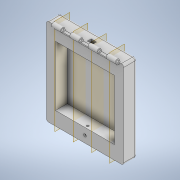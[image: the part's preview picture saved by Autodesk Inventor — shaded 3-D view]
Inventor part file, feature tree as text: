
AUTODESK INVENTOR PART (.ipt)
format: ipt  version: 2022 (Build 260153000, 153)  size: 294,912 bytes
history: native  units: in
note: dims shown in document units (in); Inventor stores cm internally (conversion verified against a paired STEP export)
features: extrude x13, sketch x13, plane x4, fillet x3, projected_geometry x3
ambient origin geometry x8: Origin, YZ Plane, XZ Plane, XY Plane, X Axis, Y Axis, Z Axis, Center Point
bodies: Solid1 (feature_tree)
feature tree (36):
  extrude  "Extrusion1"  Depth=6.6in
  extrude  "Extrusion3"  Depth=1.5in
  fillet  "Fillet1"  Radius=1.0in
  plane  "Work Plane1"
  extrude  "Extrusion4"  Depth=1.48in TaperAngle=0.0deg
  plane  "Work Plane2"
  extrude  "Extrusion5"  Depth=0.25in
  plane  "Work Plane3"
  extrude  "Extrusion6"  Depth=0.45in
  plane  "Work Plane4"
  extrude  "Extrusion7"  Depth=0.26in
  extrude  "Extrusion8"  Depth=2.01in
  extrude  "Extrusion9"  Depth=0.45in
  fillet  "Fillet2"  Radius=0.26in
  fillet  "Fillet3"  Radius=1.0in
  extrude  "Extrusion10"  Depth=0.45in
  extrude  "Extrusion11"  Depth=0.26in
  extrude  "Extrusion12"  Depth=2.01in
  extrude  "Extrusion14"  Depth=0.45in
  extrude  "Extrusion15"  Depth=0.6in TaperAngle=0.0deg
  sketch  "Sketch1"  dims[d0=6.506in d1=6.6in]
  sketch  "Sketch3"  dims[d2=1.5in d3=1.5in d4=1.0in]
  sketch  "Sketch4"  dims[d5=1.0in d6=1.48in d7=0.0in]
  sketch  "Sketch5"  dims[d10=0.185in d11=0.0in d12=0.25in]
  sketch  "Sketch6"  dims[d13=0.01in d14=0.45in]
  sketch  "Sketch7"  dims[d15=0.45in d16=0.26in]
  sketch  "Sketch9"  dims[d17=1.0in d18=0.0in d19=2.01in]
  sketch  "Sketch10"  dims[d20=0.45in d21=0.45in d22=0.26in d23=1.0in d24=0.0in]
  projected_geometry  "Projected Loop1"
  sketch  "Sketch11"  dims[d25=2.01in d26=0.45in]
  projected_geometry  "Projected Loop2"
  sketch  "Sketch13"  dims[d27=0.45in d28=0.26in]
  sketch  "Sketch14"  dims[d29=1.0in d30=0.0in d31=2.01in]
  sketch  "Sketch17"  dims[d32=0.45in d33=0.45in]
  projected_geometry  "Projected Loop6"
  sketch  "Sketch18"  dims[d34=0.26in d35=1.0in d36=0.0in d41=7.03in d42=0.0in d43=0.225in d44=0.0in d45=0.25in d46=0.125in d47=0.297in d48=4.0in d49=0.0in d50=0.317in d51=1.313in d52=0.0in d53=0.25in d54=0.75in d55=0.0in d63=0.541in d64=0.2935in d65=0.413in d66=0.6in d67=3.0in d68=0.0in d69=0.5in d70=0.1in d71=0.0in]
